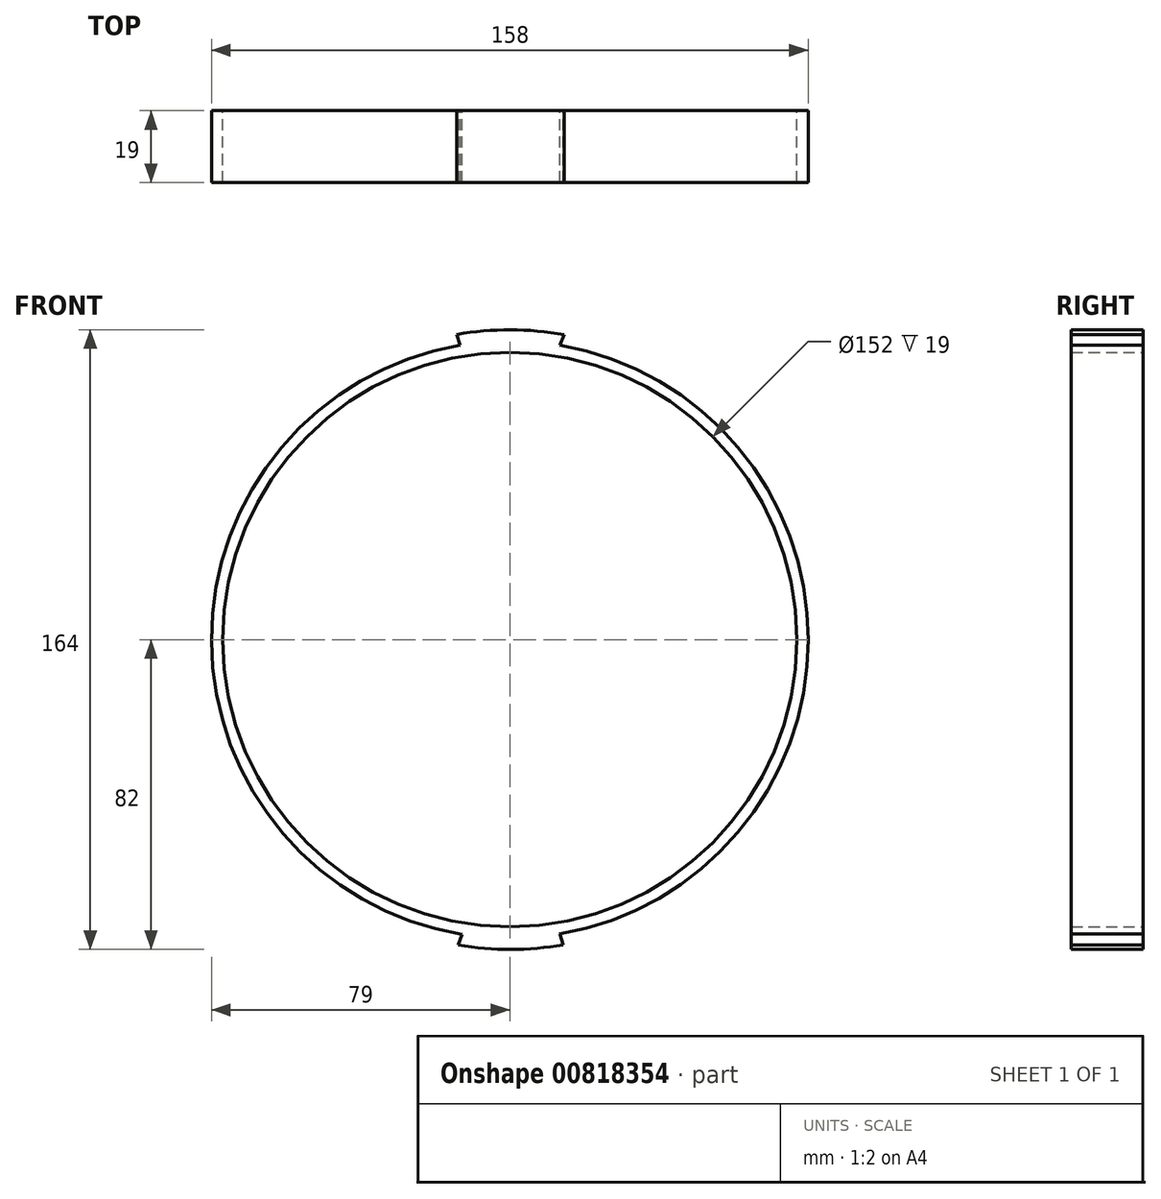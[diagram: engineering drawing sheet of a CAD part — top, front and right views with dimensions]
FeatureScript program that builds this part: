
annotation { "Feature Type Name" : "Feature", "Feature Type Description" : "" }
export const myFeature = defineFeature(function(context is Context, id is Id, definition is map)
    precondition{}
    {
        {
            var Q0;
            Q0=qCreatedBy(makeId("Front.planeOp"),FACE);
            var sketch = newSketch(context, id + "F0", { "sketchPlane" : qUnion([Q0])});
            skCircle(sketch, "E0", {"center": v(0, 0) * mm, "radius": 76 * mm});
            skCircle(sketch, "E1", {"center": v(0, 0) * mm, "radius": 79 * mm});
            skArc(sketch, "E2", {"start": v(14.33, 80.74) * mm, "mid": v(0.14, 82) * mm, "end": v(-14.07, 80.78) * mm});
            skLineSegment(sketch, "E3", {"start": v(14.33, 80.74) * mm, "end": v(12.2, 75.02) * mm});
            skLineSegment(sketch, "E4", {"start": v(-14.07, 80.78) * mm, "end": v(-12.3, 75) * mm});
            skLineSegment(sketch, "E5", {"start": v(12.21, -75.01) * mm, "end": v(14.14, -80.77) * mm});
            skLineSegment(sketch, "E6", {"start": v(-11.68, -75.1) * mm, "end": v(-13.65, -80.86) * mm});
            skArc(sketch, "E7.trimOffspring", {"start": v(-13.65, -80.86) * mm, "mid": v(0.25, -82) * mm, "end": v(14.14, -80.77) * mm});
            skPoint(sketch, "E8", {"position": v(13.18, -77.9) * mm});
            skPoint(sketch, "E8.positionSnap0", {"position": v(13.18, -77.9) * mm});
            skPoint(sketch, "E9", {"position": v(-12.67, -77.98) * mm});
            skPoint(sketch, "E9.positionSnap0", {"position": v(-12.66, -77.98) * mm});
            skSolve(sketch);
        }
        {
            var Q0;
            Q0 = qSketchRegion(id + "F0", true);
            extrude(context, id + "F1", {"entities" : qUnion([Q0]), "depth" : 19 * mm, "offsetDistance" : 25 * mm});
        }
    });
